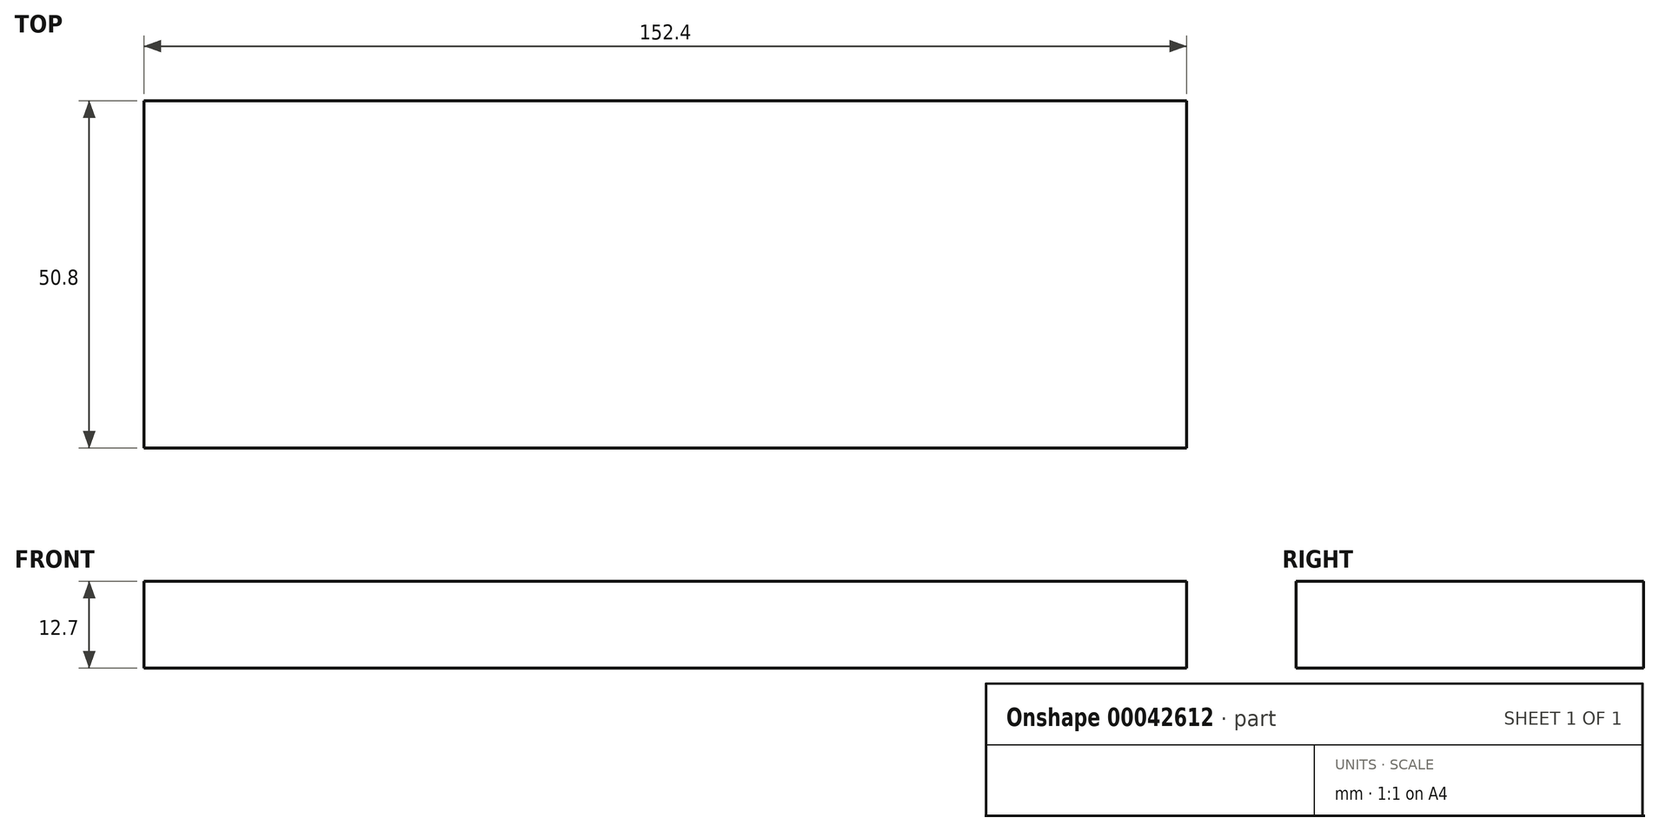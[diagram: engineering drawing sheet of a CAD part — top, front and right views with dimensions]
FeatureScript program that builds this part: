
annotation { "Feature Type Name" : "Feature", "Feature Type Description" : "" }
export const myFeature = defineFeature(function(context is Context, id is Id, definition is map)
    precondition{}
    {
        {
            var Q0;
            Q0=qCreatedBy(makeId("Top.planeOp"),FACE);
            var sketch = newSketch(context, id + "F0", { "sketchPlane" : qUnion([Q0])});
            skLineSegment(sketch, "E0.rect.bottom", {"start": v(-76.2, 25.4) * mm, "end": v(76.2, 25.4) * mm});
            skLineSegment(sketch, "E0.rect.top", {"start": v(-76.2, -25.4) * mm, "end": v(76.2, -25.4) * mm});
            skLineSegment(sketch, "E0.rect.left", {"start": v(-76.2, 25.4) * mm, "end": v(-76.2, -25.4) * mm});
            skLineSegment(sketch, "E0.rect.right", {"start": v(76.2, 25.4) * mm, "end": v(76.2, -25.4) * mm});
            skPoint(sketch, "E0.rect.middle", {"position": v(0, 0) * mm});
            skSolve(sketch);
        }
        {
            var Q0;
            Q0 = qSketchRegion(id + "F0", true);
            extrude(context, id + "F1", {"entities" : qUnion([Q0]), "depth" : 12.7 * mm});
        }
    });
